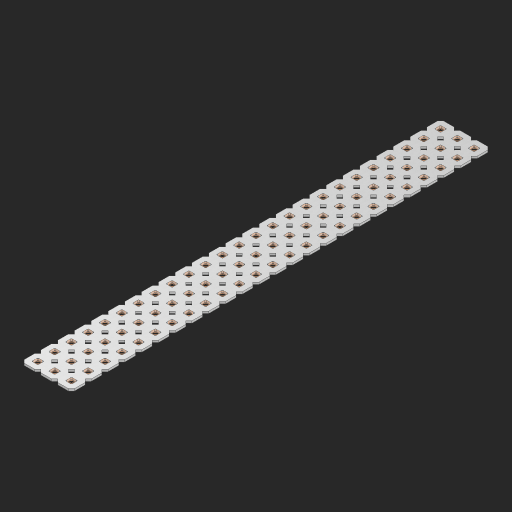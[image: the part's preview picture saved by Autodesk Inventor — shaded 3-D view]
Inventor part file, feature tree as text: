
AUTODESK INVENTOR PART (.ipt)
format: ipt  version: 2023 (Build 270158000, 158)  size: 1,147,392 bytes
history: native  units: in
note: dims shown in document units (in); Inventor stores cm internally (conversion verified against a paired STEP export)
features: other x76, extrude x74, sketch x2, pattern_linear x1
ambient origin geometry x8: Origin, YZ Plane, XZ Plane, XY Plane, X Axis, Y Axis, Z Axis, Center Point
bodies: Solid1 (feature_tree), Body (feature_tree)
feature tree (153):
  pattern_linear  "Rectangular Pattern1"  Spacing1=0.09in  [1 undecoded]
  sketch  "Sketch1"  dims[d1=0.5in]
  sketch  "Sketch2"  dims[d2=0.182in d3=0.09in d4=0.09in d5=0.09in d6=0.09in d7=0.09in d8=0.09in d9=0.09in d10=0.09in d11=0.02in d13=0.0in d14=0.172in d15=0.0625in d16=0.0in d19=0.5in d22=0.5in]
  other  "Srf1"
  other  "Srf126"
  other  "Srf127"
  other  "Srf128"
  other  "Srf129"
  other  "Srf130"
  other  "Srf131"
  other  "Srf250"
  other  "Srf251"
  other  "Srf252"
  other  "Srf253"
  other  "Srf254"
  other  "Srf255"
  other  "Srf256"
  other  "Srf257"
  other  "Srf258"
  other  "Srf259"
  other  "Srf260"
  other  "Srf261"
  other  "Srf262"
  other  "Srf263"
  other  "Srf264"
  other  "Srf265"
  other  "Srf266"
  other  "Srf267"
  other  "Srf268"
  other  "Srf269"
  other  "Srf270"
  other  "Srf271"
  other  "Srf272"
  other  "Srf273"
  other  "Srf274"
  other  "Srf275"
  other  "Srf276"
  other  "Srf277"
  other  "Srf278"
  other  "Srf279"
  other  "Srf280"
  other  "Srf281"
  other  "Srf282"
  other  "Srf283"
  other  "Srf284"
  other  "Srf285"
  other  "Srf286"
  other  "Srf287"
  other  "Srf288"
  other  "Srf289"
  other  "Srf290"
  other  "Srf291"
  other  "Srf292"
  other  "Srf293"
  other  "Srf294"
  other  "Srf295"
  other  "Srf296"
  other  "Srf297"
  other  "Srf298"
  other  "Srf299"
  other  "Srf300"
  other  "Srf301"
  other  "Srf302"
  other  "Srf303"
  other  "Srf304"
  other  "Srf305"
  other  "Srf306"
  other  "Srf307"
  other  "Srf308"
  other  "Srf309"
  other  "Srf310"
  other  "Srf311"
  other  "Srf312"
  other  "Srf313"
  other  "Srf314"
  other  "Srf315"
  other  "Srf316"
  other  "Srf317"
  other  "Circle"
  extrude  "ExtrusionSrf126"  Depth=0.09in
  extrude  "ExtrusionSrf127"  Depth=0.09in
  extrude  "ExtrusionSrf128"  Depth=0.09in
  extrude  "ExtrusionSrf129"  Depth=0.09in
  extrude  "ExtrusionSrf130"  Depth=0.09in
  extrude  "ExtrusionSrf131"  Depth=0.09in
  extrude  "ExtrusionSrf250"  Depth=0.09in
  extrude  "ExtrusionSrf251"  Depth=0.02in
  extrude  "ExtrusionSrf252"  TaperAngle=0.0deg  [1 undecoded]
  extrude  "ExtrusionSrf253"  Depth=0.5in
  extrude  "ExtrusionSrf254"  Depth=0.0625in TaperAngle=0.0deg
  extrude  "ExtrusionSrf255"  Depth=0.5in
  extrude  "ExtrusionSrf256"  Depth=0.5in
  extrude  "ExtrusionSrf257"  [1 undecoded]
  extrude  "ExtrusionSrf258"  [1 undecoded]
  extrude  "ExtrusionSrf259"  [1 undecoded]
  extrude  "ExtrusionSrf260"  [1 undecoded]
  extrude  "ExtrusionSrf261"  [1 undecoded]
  extrude  "ExtrusionSrf262"  [1 undecoded]
  extrude  "ExtrusionSrf263"  [1 undecoded]
  extrude  "ExtrusionSrf264"  [1 undecoded]
  extrude  "ExtrusionSrf265"  [1 undecoded]
  extrude  "ExtrusionSrf266"  [1 undecoded]
  extrude  "ExtrusionSrf267"  [1 undecoded]
  extrude  "ExtrusionSrf268"  [1 undecoded]
  extrude  "ExtrusionSrf269"  [1 undecoded]
  extrude  "ExtrusionSrf270"  [1 undecoded]
  extrude  "ExtrusionSrf271"  [1 undecoded]
  extrude  "ExtrusionSrf272"  [1 undecoded]
  extrude  "ExtrusionSrf273"  [1 undecoded]
  extrude  "ExtrusionSrf274"  [1 undecoded]
  extrude  "ExtrusionSrf275"  [1 undecoded]
  extrude  "ExtrusionSrf276"  [1 undecoded]
  extrude  "ExtrusionSrf277"  [1 undecoded]
  extrude  "ExtrusionSrf278"  [1 undecoded]
  extrude  "ExtrusionSrf279"  [1 undecoded]
  extrude  "ExtrusionSrf280"  [1 undecoded]
  extrude  "ExtrusionSrf281"  [1 undecoded]
  extrude  "ExtrusionSrf282"  [1 undecoded]
  extrude  "ExtrusionSrf283"  [1 undecoded]
  extrude  "ExtrusionSrf284"  [1 undecoded]
  extrude  "ExtrusionSrf285"  [1 undecoded]
  extrude  "ExtrusionSrf286"  [1 undecoded]
  extrude  "ExtrusionSrf287"  [1 undecoded]
  extrude  "ExtrusionSrf288"  [1 undecoded]
  extrude  "ExtrusionSrf289"  [1 undecoded]
  extrude  "ExtrusionSrf290"  [1 undecoded]
  extrude  "ExtrusionSrf291"  [1 undecoded]
  extrude  "ExtrusionSrf292"  [1 undecoded]
  extrude  "ExtrusionSrf293"  [1 undecoded]
  extrude  "ExtrusionSrf294"  [1 undecoded]
  extrude  "ExtrusionSrf295"  [1 undecoded]
  extrude  "ExtrusionSrf296"  [1 undecoded]
  extrude  "ExtrusionSrf297"  [1 undecoded]
  extrude  "ExtrusionSrf298"  [1 undecoded]
  extrude  "ExtrusionSrf299"  [1 undecoded]
  extrude  "ExtrusionSrf300"  [1 undecoded]
  extrude  "ExtrusionSrf301"  [1 undecoded]
  extrude  "ExtrusionSrf302"  [1 undecoded]
  extrude  "ExtrusionSrf303"  [1 undecoded]
  extrude  "ExtrusionSrf304"  [1 undecoded]
  extrude  "ExtrusionSrf305"  [1 undecoded]
  extrude  "ExtrusionSrf306"  [1 undecoded]
  extrude  "ExtrusionSrf307"  [1 undecoded]
  extrude  "ExtrusionSrf308"  [1 undecoded]
  extrude  "ExtrusionSrf309"  [1 undecoded]
  extrude  "ExtrusionSrf310"  [1 undecoded]
  extrude  "ExtrusionSrf311"  [1 undecoded]
  extrude  "ExtrusionSrf312"  [1 undecoded]
  extrude  "ExtrusionSrf313"  [1 undecoded]
  extrude  "ExtrusionSrf314"  [1 undecoded]
  extrude  "ExtrusionSrf315"  [1 undecoded]
  extrude  "ExtrusionSrf316"  [1 undecoded]
  extrude  "ExtrusionSrf317"  [1 undecoded]
note: 63 required parameter values undecoded (feature->parameter linkage not recoverable at this tier; creation-order binding heuristic only, values carry confidence <= 0.55)
